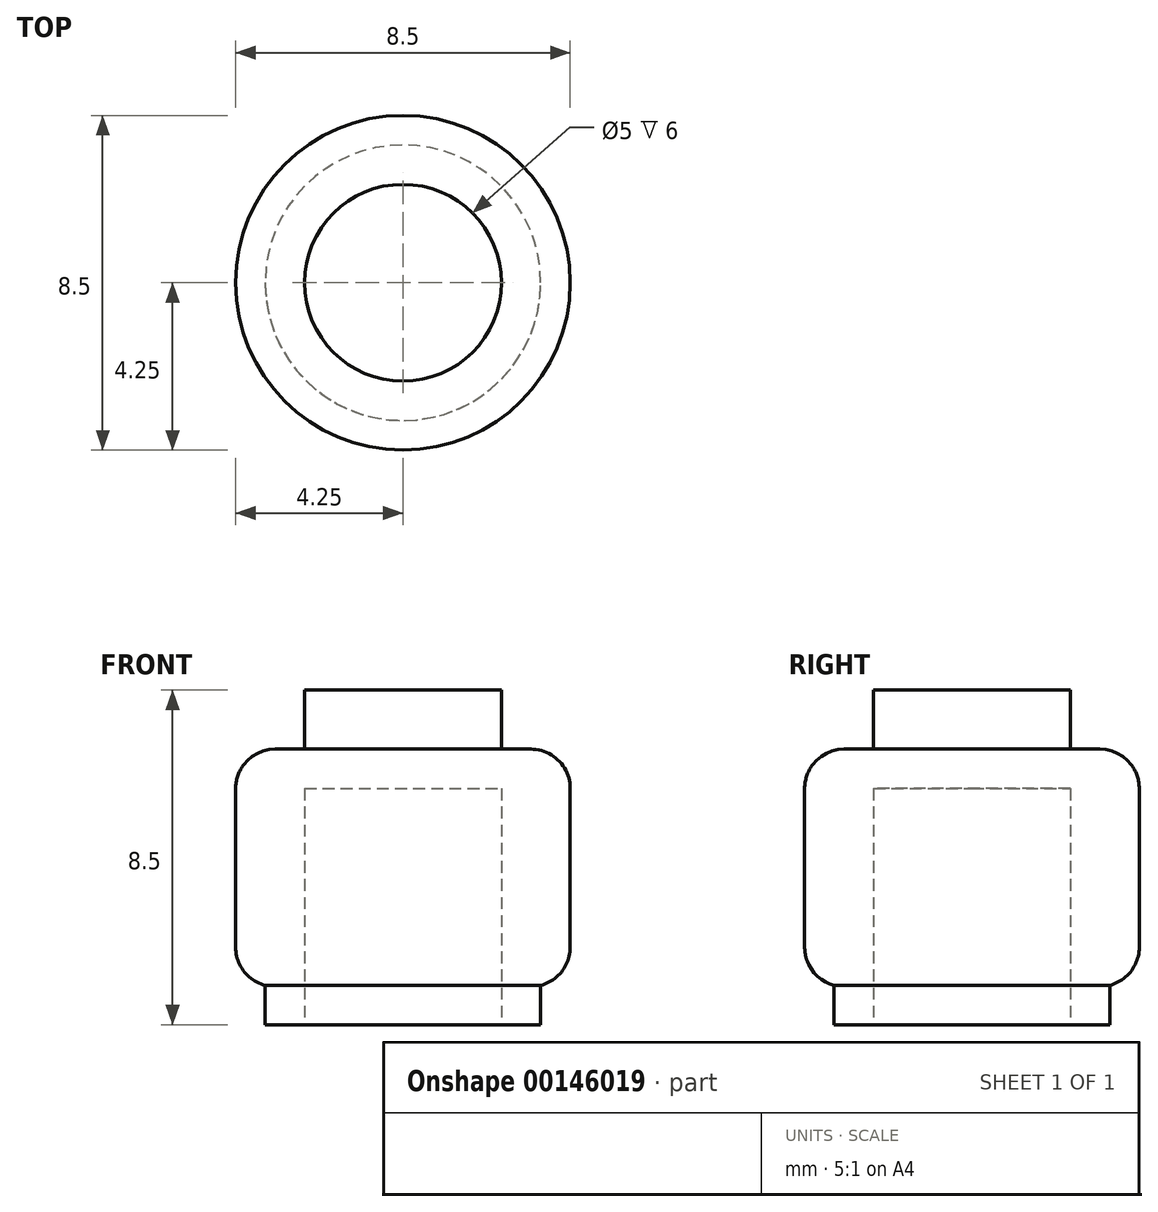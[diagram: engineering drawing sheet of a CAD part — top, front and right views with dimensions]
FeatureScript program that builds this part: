
annotation { "Feature Type Name" : "Feature", "Feature Type Description" : "" }
export const myFeature = defineFeature(function(context is Context, id is Id, definition is map)
    precondition{}
    {
        {
            var Q0;
            Q0=qCreatedBy(makeId("Top.planeOp"),FACE);
            var sketch = newSketch(context, id + "F0", { "sketchPlane" : qUnion([Q0])});
            skCircle(sketch, "E0", {"center": v(0, 0) * mm, "radius": 3.5 * mm});
            skSolve(sketch);
        }
        {
            var Q0;
            Q0=qSketchRegion(id+"F0",true);
            extrude(context, id + "F1", {"entities" : qUnion([Q0]), "depth" : 1 * mm});
        }
        {
            var Q0;
            Q0=makeQuery(id+"F1.opExtrude","CAP_FACE",FACE,{"disambiguationData":[OSD([sQuery(id+"F0.wireOp",EDGE,"E0")])],"isStart":false});
            var sketch = newSketch(context, id + "F2", { "sketchPlane" : qUnion([Q0])});
            skCircle(sketch, "E1", {"center": v(0, 0) * mm, "radius": 4.25 * mm});
            skSolve(sketch);
        }
        {
            var Q0;
            Q0=qSketchRegion(id+"F2",true);
            extrude(context, id + "F3", {"entities" : qUnion([Q0]), "operationType" : NewBodyOperationType.ADD, "depth" : 6 * mm});
        }
        {
            var Q0;
            Q0=makeQuery(id+"F3.opExtrude","CAP_FACE",FACE,{"disambiguationData":[OSD([sQuery(id+"F2.wireOp",EDGE,"E1")])],"isStart":false});
            var sketch = newSketch(context, id + "F4", { "sketchPlane" : qUnion([Q0])});
            skCircle(sketch, "E2", {"center": v(0, 0) * mm, "radius": 2.5 * mm});
            skSolve(sketch);
        }
        {
            var Q0;
            Q0=qSketchRegion(id+"F4",true);
            extrude(context, id + "F5", {"entities" : qUnion([Q0]), "operationType" : NewBodyOperationType.ADD, "depth" : 1.5 * mm});
        }
        {
            var Q0;
            Q0=makeQuery(id+"F3.opExtrude","CAP_EDGE",EDGE,{"disambiguationData":[OSD([sQuery(id+"F2.wireOp",EDGE,"E1")])],"isStart":false});
            var Q1;
            Q1=makeQuery(id+"F3.opExtrude","CAP_EDGE",EDGE,{"disambiguationData":[OSD([sQuery(id+"F2.wireOp",EDGE,"E1")])],"isStart":true});
            fillet(context, id + "F6", {"entities" : qUnion([Q0, Q1]), "radius" : 1 * mm, "tangentPropagation" : true, "allowEdgeOverflow" : false});
        }
        {
            var Q0;
            Q0=makeQuery(id+"F1.opExtrude","CAP_FACE",FACE,{"disambiguationData":[OSD([sQuery(id+"F0.wireOp",EDGE,"E0")])],"isStart":true});
            var sketch = newSketch(context, id + "F7", { "sketchPlane" : qUnion([Q0])});
            skCircle(sketch, "E3", {"center": v(0, 0) * mm, "radius": 2.5 * mm});
            skSolve(sketch);
        }
        {
            var Q0;
            Q0=qSketchRegion(id+"F7",true);
            extrude(context, id + "F8", {"entities" : qUnion([Q0]), "operationType" : NewBodyOperationType.REMOVE, "oppositeDirection" : true, "depth" : 6 * mm});
        }
    });
